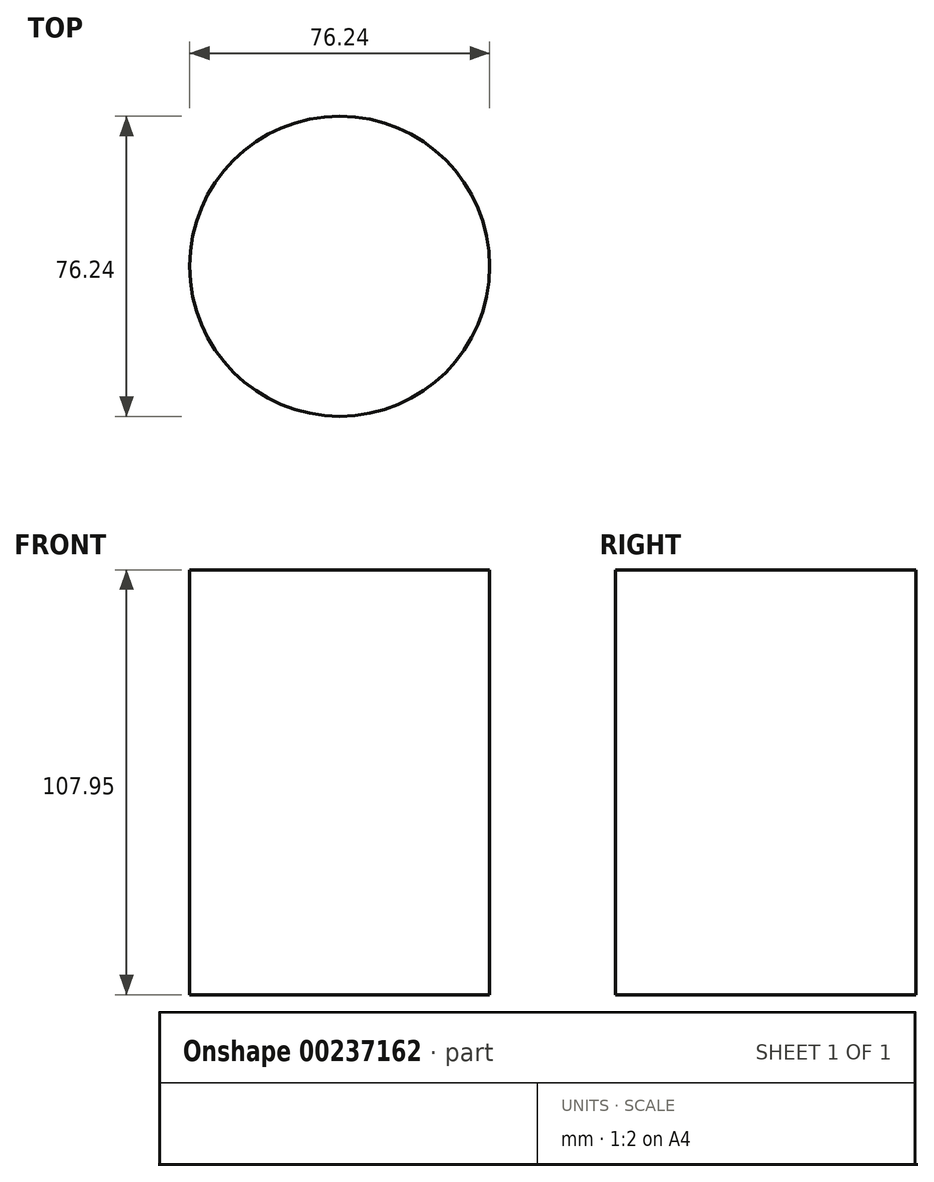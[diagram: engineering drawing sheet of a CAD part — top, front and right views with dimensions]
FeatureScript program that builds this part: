
annotation { "Feature Type Name" : "Feature", "Feature Type Description" : "" }
export const myFeature = defineFeature(function(context is Context, id is Id, definition is map)
    precondition{}
    {
        {
            var Q0;
            Q0=qCreatedBy(makeId("Top.planeOp"),FACE);
            var sketch = newSketch(context, id + "F0", { "sketchPlane" : qUnion([Q0])});
            skCircle(sketch, "E0", {"center": v(0, 0) * mm, "radius": 38.12 * mm});
            skSolve(sketch);
        }
        {
            var Q0;
            Q0=qCreatedBy(makeId("Right.planeOp"),FACE);
            var sketch = newSketch(context, id + "F1", { "sketchPlane" : qUnion([Q0])});
            skSolve(sketch);
        }
        {
            var Q0;
            Q0 = qSketchRegion(id + "F1", true);
            var Q1;
            Q1 = qSketchRegion(id + "F0", true);
            extrude(context, id + "F2", {"entities" : qUnion([Q0, Q1]), "depth" : 107.95 * mm});
        }
    });
